# Revit family: BFS_Plumbing_Valves_hansgrohe_74997XXX-Zesis-S-Shut-off-valve_concealed-installation
name_source: partatom
category: Plumbing Fixtures
units: mm (PartAtom-declared; Revit-internal decimal feet)

## family parameters
Cut with Voids When Loaded = No
Host = Face
Maintain Annotation Orientation = No
OmniClass Number = 23.27.31.00
OmniClass Title = Valves
Part Type = Normal
Room Calculation Point = No
Round Connector Dimension = Use Diameter
Shared = No

## types (1)
- 000 Chrome
    Default Elevation = 0 mm  [stored 0 ft]
    Description = Zesis S Shut-off valve for concealed installation
    Manufacturer = Hansgrohe
    Material 1 = Hansgrohe - Metal - 000 Chrome
    Model = 74997XXX
    Product Page URL = https://www.hansgrohe.com
    Product data url = https://www.bimobject.com
    URL = https://www.hansgrohe.com
    Version = 1

note: [stored X ft] marks values corroborated as IEEE doubles in the binary element streams (Revit-internal decimal feet)

## geometry (parser evidence)
native form markers: Sweep x2
no freeform markers — native parametric forms only
